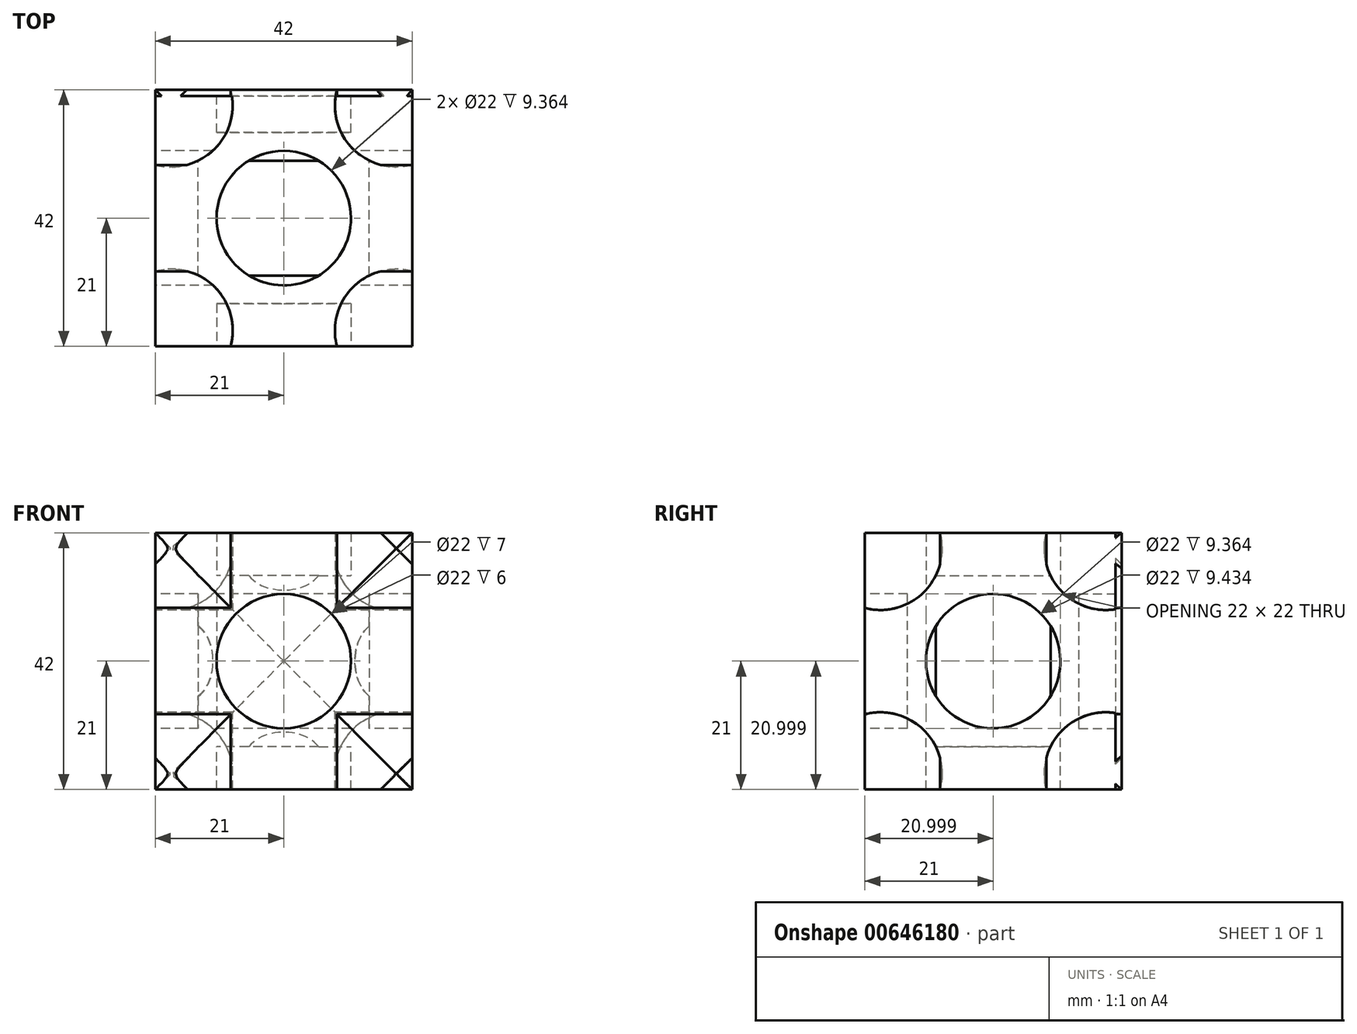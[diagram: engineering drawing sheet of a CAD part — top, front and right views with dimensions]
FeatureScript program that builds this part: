
annotation { "Feature Type Name" : "Feature", "Feature Type Description" : "" }
export const myFeature = defineFeature(function(context is Context, id is Id, definition is map)
    precondition{}
    {
        {
            var Q0;
            Q0=qCreatedBy(makeId("Top.planeOp"),FACE);
            var sketch = newSketch(context, id + "F0", { "sketchPlane" : qUnion([Q0])});
            skCircle(sketch, "E0", {"center": v(0, 0) * mm, "radius": 11 * mm});
            skPoint(sketch, "E1.0.midPoint", {"position": v(0, 21) * mm});
            skLineSegment(sketch, "E2", {"start": v(0, 21) * mm, "end": v(0, 11) * mm, "construction": true});
            skLineSegment(sketch, "E3", {"start": v(21, -0.1) * mm, "end": v(11, -0.1) * mm, "construction": true});
            skLineSegment(sketch, "E4", {"start": v(0, -11) * mm, "end": v(0, -21) * mm, "construction": true});
            skLineSegment(sketch, "E5", {"start": v(-21, -0.52) * mm, "end": v(-11, -0.27) * mm, "construction": true});
            skPoint(sketch, "E6.orphan", {"position": v(8.73, 20.99) * mm});
            skPoint(sketch, "E7.orphan", {"position": v(21.02, 8.65) * mm});
            skPoint(sketch, "E1.2.end.orphan", {"position": v(20.98, -8.85) * mm});
            skPoint(sketch, "E8.orphan", {"position": v(7.4, -20.44) * mm});
            skPoint(sketch, "E9.orphan", {"position": v(-7.4, -21.56) * mm});
            skPoint(sketch, "E10.orphan", {"position": v(-20.83, -9.53) * mm});
            skPoint(sketch, "E1.6.end.orphan", {"position": v(-21.15, 8.5) * mm});
            skPoint(sketch, "E1.0.start.orphan", {"position": v(-8.73, 21.01) * mm});
            skArc(sketch, "E11.cCircle", {"start": v(-19.25, 8.4) * mm, "mid": v(-21, 0) * mm, "end": v(-19.25, -8.39) * mm, "construction": true});
            skLineSegment(sketch, "E11.0", {"start": v(-8.7, 21) * mm, "end": v(8.7, 21) * mm});
            skLineSegment(sketch, "E11.2", {"start": v(21, 8.7) * mm, "end": v(21, -8.7) * mm});
            skLineSegment(sketch, "E11.4", {"start": v(8.7, -21) * mm, "end": v(-8.7, -21) * mm});
            skLineSegment(sketch, "E11.6", {"start": v(-21, -8.7) * mm, "end": v(-21, 8.7) * mm});
            skLineSegment(sketch, "E12", {"start": v(7.78, -7.78) * mm, "end": v(11.31, -11.31) * mm, "construction": true});
            skLineSegment(sketch, "E13", {"start": v(-7.4, -8.14) * mm, "end": v(-10.76, -11.84) * mm, "construction": true});
            skLineSegment(sketch, "E14", {"start": v(-7.83, 7.73) * mm, "end": v(-11.39, 11.24) * mm, "construction": true});
            skLineSegment(sketch, "E15", {"start": v(7.8, 7.76) * mm, "end": v(11.34, 11.3) * mm, "construction": true});
            skPoint(sketch, "E16.endSnap0", {"position": v(14.85, -14.85) * mm});
            skArc(sketch, "E17", {"start": v(-8.7, -21) * mm, "mid": v(-11.28, -11.28) * mm, "end": v(-21, -8.7) * mm});
            skArc(sketch, "E18", {"start": v(-21, 8.7) * mm, "mid": v(-11.31, 11.31) * mm, "end": v(-8.7, 21) * mm});
            skArc(sketch, "E19", {"start": v(21, -8.7) * mm, "mid": v(11.31, -11.31) * mm, "end": v(8.7, -21) * mm});
            skArc(sketch, "E20", {"start": v(8.7, 21) * mm, "mid": v(11.31, 11.31) * mm, "end": v(21, 8.7) * mm});
            skArc(sketch, "E21.trimOffspring", {"start": v(8.4, 19.25) * mm, "mid": v(0, 21) * mm, "end": v(-8.4, 19.25) * mm, "construction": true});
            skArc(sketch, "E22.trimOffspring", {"start": v(19.25, -8.4) * mm, "mid": v(21, 0) * mm, "end": v(19.25, 8.4) * mm, "construction": true});
            skArc(sketch, "E23.trimOffspring", {"start": v(-8.39, -19.25) * mm, "mid": v(0, -21) * mm, "end": v(8.4, -19.25) * mm, "construction": true});
            skSolve(sketch);
        }
        {
            var Q0;
            Q0=qCreatedBy(makeId("Right.planeOp"),FACE);
            var sketch = newSketch(context, id + "F1", { "sketchPlane" : qUnion([Q0])});
            skCircle(sketch, "E24", {"center": v(0, 0) * mm, "radius": 11 * mm});
            skCircle(sketch, "E25.cCircle", {"center": v(0, 0) * mm, "radius": 21 * mm, "construction": true});
            skLineSegment(sketch, "E25.0", {"start": v(-8.7, 21) * mm, "end": v(8.7, 21) * mm});
            skLineSegment(sketch, "E25.2", {"start": v(21, 8.7) * mm, "end": v(21, -8.7) * mm});
            skLineSegment(sketch, "E25.4", {"start": v(8.7, -21) * mm, "end": v(-8.7, -21) * mm});
            skLineSegment(sketch, "E25.6", {"start": v(-21, -8.7) * mm, "end": v(-21, 8.7) * mm});
            skPoint(sketch, "E25.0.midPoint", {"position": v(0, 21) * mm});
            skLineSegment(sketch, "E26", {"start": v(-14.85, 14.85) * mm, "end": v(-7.78, 7.78) * mm, "construction": true});
            skLineSegment(sketch, "E27", {"start": v(-14.85, -14.85) * mm, "end": v(-7.78, -7.78) * mm, "construction": true});
            skLineSegment(sketch, "E28", {"start": v(14.85, -14.85) * mm, "end": v(7.78, -7.78) * mm, "construction": true});
            skLineSegment(sketch, "E29", {"start": v(14.85, 14.85) * mm, "end": v(7.78, 7.78) * mm, "construction": true});
            skLineSegment(sketch, "E30", {"start": v(14.85, 14.85) * mm, "end": v(11.31, 11.31) * mm, "construction": true});
            skLineSegment(sketch, "E31", {"start": v(11.31, 11.31) * mm, "end": v(11.31, -11.31) * mm, "construction": true});
            skLineSegment(sketch, "E32", {"start": v(11.31, -11.31) * mm, "end": v(-11.31, -11.31) * mm, "construction": true});
            skLineSegment(sketch, "E33", {"start": v(-11.31, -11.31) * mm, "end": v(-11.31, 11.31) * mm, "construction": true});
            skLineSegment(sketch, "E34", {"start": v(-11.31, 11.31) * mm, "end": v(11.31, 11.31) * mm, "construction": true});
            skArc(sketch, "E35", {"start": v(21, -8.7) * mm, "mid": v(11.31, -11.31) * mm, "end": v(8.7, -21) * mm});
            skArc(sketch, "E36", {"start": v(8.7, 21) * mm, "mid": v(11.31, 11.31) * mm, "end": v(21, 8.7) * mm});
            skArc(sketch, "E37", {"start": v(-21, 8.7) * mm, "mid": v(-11.31, 11.31) * mm, "end": v(-8.7, 21) * mm});
            skArc(sketch, "E38", {"start": v(-8.7, -21) * mm, "mid": v(-11.31, -11.31) * mm, "end": v(-21, -8.7) * mm});
            skSolve(sketch);
        }
        {
            var Q0;
            Q0 = qSketchRegion(id + "F1", true);
            extrude(context, id + "F2", {"entities" : qUnion([Q0]), "depth" : 21 * mm, "offsetDistance" : 25 * mm});
        }
        {
            var Q0;
            Q0=makeQuery(id+"F2.opExtrude","CAP_FACE",FACE,{"disambiguationData":[OSD([sQuery(id+"F1.wireOp",EDGE,"E24"),sQuery(id+"F1.wireOp",EDGE,"E25.0"),sQuery(id+"F1.wireOp",EDGE,"E25.1"),sQuery(id+"F1.wireOp",EDGE,"E25.2"),sQuery(id+"F1.wireOp",EDGE,"E25.3"),sQuery(id+"F1.wireOp",EDGE,"E25.4"),sQuery(id+"F1.wireOp",EDGE,"E25.5"),sQuery(id+"F1.wireOp",EDGE,"E25.6"),sQuery(id+"F1.wireOp",EDGE,"E25.7")])],"isStart":true});
            extrude(context, id + "F3", {"entities" : qUnion([Q0]), "operationType" : NewBodyOperationType.ADD, "depth" : 21 * mm, "offsetDistance" : 25 * mm});
        }
        {
            var Q0;
            Q0 = qSketchRegion(id + "F0", true);
            extrude(context, id + "F4", {"entities" : qUnion([Q0]), "operationType" : NewBodyOperationType.ADD, "depth" : 21 * mm, "offsetDistance" : 25 * mm});
        }
        {
            var Q0;
            Q0 = qSketchRegion(id + "F0", true);
            extrude(context, id + "F5", {"entities" : qUnion([Q0]), "operationType" : NewBodyOperationType.ADD, "oppositeDirection" : true, "depth" : 21 * mm, "offsetDistance" : 25 * mm});
        }
        {
            var Q0;
            {var subQ0=sQuery(id+"F1.wireOp",EDGE,"E25.4");Q0=makeQuery(id+"F5.boolean.opBoolean","MERGE",FACE,{"derivedFrom":[makeQuery(id+"F3.boolean.opBoolean","MERGE",FACE,{"derivedFrom":[makeQuery(id+"F2.opExtrude","SWEPT_FACE",FACE,{"disambiguationData":[OSD([subQ0])]}),makeQuery(id+"F3.opExtrude","SWEPT_FACE",FACE,{"disambiguationData":[OSD([subQ0])]})]}),makeQuery(id+"F5.opExtrude","CAP_FACE",FACE,{"disambiguationData":[OSD([sQuery(id+"F0.wireOp",EDGE,"E0"),sQuery(id+"F0.wireOp",EDGE,"E11.0"),sQuery(id+"F0.wireOp",EDGE,"E11.1"),sQuery(id+"F0.wireOp",EDGE,"E11.2"),sQuery(id+"F0.wireOp",EDGE,"E11.3"),sQuery(id+"F0.wireOp",EDGE,"E11.4"),sQuery(id+"F0.wireOp",EDGE,"E11.5"),sQuery(id+"F0.wireOp",EDGE,"E11.6"),sQuery(id+"F0.wireOp",EDGE,"E11.7")])],"isStart":false})]});}
            var sketch = newSketch(context, id + "F6", { "sketchPlane" : qUnion([Q0])});
            skCircle(sketch, "E39", {"center": v(0, 0) * mm, "radius": 11 * mm});
            skSolve(sketch);
        }
        {
            var Q0;
            {var subQ1=sQuery(id+"F1.wireOp",EDGE,"E25.4");var subQ2=sQuery(id+"F1.wireOp",EDGE,"E25.3");var subQ3=makeQuery(id+"F3.boolean.opBoolean","MERGE",EDGE,{"derivedFrom":[makeQuery(id+"F2.opExtrude","SWEPT_EDGE",EDGE,{"disambiguationData":[OSD([subQ2,subQ1])]}),makeQuery(id+"F3.opExtrude","SWEPT_EDGE",EDGE,{"disambiguationData":[OSD([subQ2,subQ1])]})]});Q0=makeQuery(id+"F6.imprint","IMPRINT",FACE,{"disambiguationData":[TD([[makeQuery(id+"F6.imprint","IMPRINT",EDGE,{"derivedFrom":subQ3}),1.0]])]});}
            var Q1;
            {var subQ1=sQuery(id+"F1.wireOp",EDGE,"E25.5");var subQ2=sQuery(id+"F1.wireOp",EDGE,"E25.4");var subQ3=makeQuery(id+"F3.boolean.opBoolean","MERGE",EDGE,{"derivedFrom":[makeQuery(id+"F2.opExtrude","SWEPT_EDGE",EDGE,{"disambiguationData":[OSD([subQ2,subQ1])]}),makeQuery(id+"F3.opExtrude","SWEPT_EDGE",EDGE,{"disambiguationData":[OSD([subQ2,subQ1])]})]});Q1=makeQuery(id+"F6.imprint","IMPRINT",FACE,{"disambiguationData":[TD([[makeQuery(id+"F6.imprint","IMPRINT",EDGE,{"derivedFrom":subQ3}),-1.0]])]});}
            var Q2;
            {var subQ1=sQuery(id+"F1.wireOp",EDGE,"E25.4");var subQ2=sQuery(id+"F1.wireOp",EDGE,"E25.3");var subQ3=makeQuery(id+"F3.boolean.opBoolean","MERGE",EDGE,{"derivedFrom":[makeQuery(id+"F2.opExtrude","SWEPT_EDGE",EDGE,{"disambiguationData":[OSD([subQ2,subQ1])]}),makeQuery(id+"F3.opExtrude","SWEPT_EDGE",EDGE,{"disambiguationData":[OSD([subQ2,subQ1])]})]});Q2=makeQuery(id+"F6.imprint","IMPRINT",FACE,{"disambiguationData":[TD([[makeQuery(id+"F6.imprint","IMPRINT",EDGE,{"derivedFrom":subQ3}),-1.0]])]});}
            var Q3;
            Q3=sQuery(id+"F6.wireOp",EDGE,"E39");
            extrude(context, id + "F7", {"entities" : qUnion([Q0, Q1, Q2]), "operationType" : NewBodyOperationType.REMOVE, "surfaceEntities" : qUnion([Q3]), "oppositeDirection" : true, "depth" : 7 * mm, "offsetDistance" : 25 * mm});
        }
        {
            var Q0;
            {var subQ0=sQuery(id+"F0.wireOp",EDGE,"E11.4");var subQ1=sQuery(id+"F1.wireOp",EDGE,"E25.6");Q0=makeQuery(id+"F5.boolean.opBoolean","MERGE",FACE,{"derivedFrom":[makeQuery(id+"F4.boolean.opBoolean","MERGE",FACE,{"derivedFrom":[makeQuery(id+"F3.boolean.opBoolean","MERGE",FACE,{"derivedFrom":[makeQuery(id+"F2.opExtrude","SWEPT_FACE",FACE,{"disambiguationData":[OSD([subQ1])]}),makeQuery(id+"F3.opExtrude","SWEPT_FACE",FACE,{"disambiguationData":[OSD([subQ1])]})]}),makeQuery(id+"F4.opExtrude","SWEPT_FACE",FACE,{"disambiguationData":[OSD([subQ0])]})]}),makeQuery(id+"F5.opExtrude","SWEPT_FACE",FACE,{"disambiguationData":[OSD([subQ0])]})]});}
            var sketch = newSketch(context, id + "F8", { "sketchPlane" : qUnion([Q0])});
            skCircle(sketch, "E40", {"center": v(0, 0) * mm, "radius": 11 * mm});
            skSolve(sketch);
        }
        {
            var Q0;
            Q0 = qSketchRegion(id + "F8", true);
            extrude(context, id + "F9", {"entities" : qUnion([Q0]), "operationType" : NewBodyOperationType.REMOVE, "oppositeDirection" : true, "depth" : 7 * mm, "offsetDistance" : 25 * mm});
        }
        {
            var Q0;
            {var subQ0=sQuery(id+"F0.wireOp",EDGE,"E11.0");var subQ1=sQuery(id+"F1.wireOp",EDGE,"E25.2");Q0=makeQuery(id+"F5.boolean.opBoolean","MERGE",FACE,{"derivedFrom":[makeQuery(id+"F4.boolean.opBoolean","MERGE",FACE,{"derivedFrom":[makeQuery(id+"F3.boolean.opBoolean","MERGE",FACE,{"derivedFrom":[makeQuery(id+"F2.opExtrude","SWEPT_FACE",FACE,{"disambiguationData":[OSD([subQ1])]}),makeQuery(id+"F3.opExtrude","SWEPT_FACE",FACE,{"disambiguationData":[OSD([subQ1])]})]}),makeQuery(id+"F4.opExtrude","SWEPT_FACE",FACE,{"disambiguationData":[OSD([subQ0])]})]}),makeQuery(id+"F5.opExtrude","SWEPT_FACE",FACE,{"disambiguationData":[OSD([subQ0])]})]});}
            var sketch = newSketch(context, id + "F10", { "sketchPlane" : qUnion([Q0])});
            skCircle(sketch, "E41", {"center": v(0, 0) * mm, "radius": 11 * mm});
            skSolve(sketch);
        }
        {
            var Q0;
            {var subQ0=sQuery(id+"F0.wireOp",EDGE,"E11.2");Q0=makeQuery(id+"F5.boolean.opBoolean","MERGE",FACE,{"derivedFrom":[makeQuery(id+"F4.boolean.opBoolean","MERGE",FACE,{"derivedFrom":[makeQuery(id+"F2.opExtrude","CAP_FACE",FACE,{"disambiguationData":[OSD([sQuery(id+"F1.wireOp",EDGE,"E24"),sQuery(id+"F1.wireOp",EDGE,"E25.0"),sQuery(id+"F1.wireOp",EDGE,"E25.1"),sQuery(id+"F1.wireOp",EDGE,"E25.2"),sQuery(id+"F1.wireOp",EDGE,"E25.3"),sQuery(id+"F1.wireOp",EDGE,"E25.4"),sQuery(id+"F1.wireOp",EDGE,"E25.5"),sQuery(id+"F1.wireOp",EDGE,"E25.6"),sQuery(id+"F1.wireOp",EDGE,"E25.7")])],"isStart":false}),makeQuery(id+"F4.opExtrude","SWEPT_FACE",FACE,{"disambiguationData":[OSD([subQ0])]})]}),makeQuery(id+"F5.opExtrude","SWEPT_FACE",FACE,{"disambiguationData":[OSD([subQ0])]})]});}
            var sketch = newSketch(context, id + "F11", { "sketchPlane" : qUnion([Q0])});
            skCircle(sketch, "E42", {"center": v(0, 0) * mm, "radius": 11 * mm});
            skSolve(sketch);
        }
        {
            var Q0;
            {var subQ0=sQuery(id+"F1.wireOp",EDGE,"E25.0");Q0=makeQuery(id+"F4.boolean.opBoolean","MERGE",FACE,{"derivedFrom":[makeQuery(id+"F3.boolean.opBoolean","MERGE",FACE,{"derivedFrom":[makeQuery(id+"F2.opExtrude","SWEPT_FACE",FACE,{"disambiguationData":[OSD([subQ0])]}),makeQuery(id+"F3.opExtrude","SWEPT_FACE",FACE,{"disambiguationData":[OSD([subQ0])]})]}),makeQuery(id+"F4.opExtrude","CAP_FACE",FACE,{"disambiguationData":[OSD([sQuery(id+"F0.wireOp",EDGE,"E0"),sQuery(id+"F0.wireOp",EDGE,"E11.0"),sQuery(id+"F0.wireOp",EDGE,"E11.1"),sQuery(id+"F0.wireOp",EDGE,"E11.2"),sQuery(id+"F0.wireOp",EDGE,"E11.3"),sQuery(id+"F0.wireOp",EDGE,"E11.4"),sQuery(id+"F0.wireOp",EDGE,"E11.5"),sQuery(id+"F0.wireOp",EDGE,"E11.6"),sQuery(id+"F0.wireOp",EDGE,"E11.7")])],"isStart":false})]});}
            var sketch = newSketch(context, id + "F12", { "sketchPlane" : qUnion([Q0])});
            skCircle(sketch, "E43", {"center": v(0, 0) * mm, "radius": 11 * mm});
            skSolve(sketch);
        }
        {
            var Q0;
            {var subQ0=sQuery(id+"F0.wireOp",EDGE,"E11.6");Q0=makeQuery(id+"F5.boolean.opBoolean","MERGE",FACE,{"derivedFrom":[makeQuery(id+"F4.boolean.opBoolean","MERGE",FACE,{"derivedFrom":[makeQuery(id+"F3.opExtrude","CAP_FACE",FACE,{"disambiguationData":[OSD([sQuery(id+"F1.wireOp",EDGE,"E24"),sQuery(id+"F1.wireOp",EDGE,"E25.0"),sQuery(id+"F1.wireOp",EDGE,"E25.1"),sQuery(id+"F1.wireOp",EDGE,"E25.2"),sQuery(id+"F1.wireOp",EDGE,"E25.3"),sQuery(id+"F1.wireOp",EDGE,"E25.4"),sQuery(id+"F1.wireOp",EDGE,"E25.5"),sQuery(id+"F1.wireOp",EDGE,"E25.6"),sQuery(id+"F1.wireOp",EDGE,"E25.7")])],"isStart":false}),makeQuery(id+"F4.opExtrude","SWEPT_FACE",FACE,{"disambiguationData":[OSD([subQ0])]})]}),makeQuery(id+"F5.opExtrude","SWEPT_FACE",FACE,{"disambiguationData":[OSD([subQ0])]})]});}
            var sketch = newSketch(context, id + "F13", { "sketchPlane" : qUnion([Q0])});
            skCircle(sketch, "E44", {"center": v(0, 0) * mm, "radius": 11 * mm});
            skSolve(sketch);
        }
        {
            var Q0;
            Q0 = qSketchRegion(id + "F13", true);
            extrude(context, id + "F14", {"entities" : qUnion([Q0]), "operationType" : NewBodyOperationType.REMOVE, "oppositeDirection" : true, "depth" : 7 * mm, "offsetDistance" : 25 * mm});
        }
        {
            var Q0;
            Q0 = qSketchRegion(id + "F10", true);
            extrude(context, id + "F15", {"entities" : qUnion([Q0]), "operationType" : NewBodyOperationType.REMOVE, "oppositeDirection" : true, "depth" : 7 * mm, "offsetDistance" : 25 * mm});
        }
        {
            var Q0;
            Q0 = qSketchRegion(id + "F11", true);
            extrude(context, id + "F16", {"entities" : qUnion([Q0]), "operationType" : NewBodyOperationType.REMOVE, "oppositeDirection" : true, "depth" : 7 * mm, "offsetDistance" : 25 * mm});
        }
        {
            var Q0;
            Q0 = qSketchRegion(id + "F12", true);
            extrude(context, id + "F17", {"entities" : qUnion([Q0]), "operationType" : NewBodyOperationType.REMOVE, "oppositeDirection" : true, "depth" : 7 * mm, "offsetDistance" : 25 * mm});
        }
        {
            var Q0;
            {var subQ0=sQuery(id+"F1.wireOp",EDGE,"E25.4");Q0=makeQuery(id+"F5.boolean.opBoolean","MERGE",FACE,{"derivedFrom":[makeQuery(id+"F3.boolean.opBoolean","MERGE",FACE,{"derivedFrom":[makeQuery(id+"F2.opExtrude","SWEPT_FACE",FACE,{"disambiguationData":[OSD([subQ0])]}),makeQuery(id+"F3.opExtrude","SWEPT_FACE",FACE,{"disambiguationData":[OSD([subQ0])]})]}),makeQuery(id+"F5.opExtrude","CAP_FACE",FACE,{"disambiguationData":[OSD([sQuery(id+"F0.wireOp",EDGE,"E0"),sQuery(id+"F0.wireOp",EDGE,"E11.0"),sQuery(id+"F0.wireOp",EDGE,"E11.2"),sQuery(id+"F0.wireOp",EDGE,"E11.4"),sQuery(id+"F0.wireOp",EDGE,"E11.6"),sQuery(id+"F0.wireOp",EDGE,"E17"),sQuery(id+"F0.wireOp",EDGE,"E18"),sQuery(id+"F0.wireOp",EDGE,"E19"),sQuery(id+"F0.wireOp",EDGE,"E20")])],"isStart":false})]});}
            var sketch = newSketch(context, id + "F18", { "sketchPlane" : qUnion([Q0])});
            skCircle(sketch, "E45", {"center": v(0, 0) * mm, "radius": 11 * mm});
            skSolve(sketch);
        }
        {
            var Q0;
            Q0 = qSketchRegion(id + "F18", true);
            extrude(context, id + "F19", {"entities" : qUnion([Q0]), "operationType" : NewBodyOperationType.REMOVE, "oppositeDirection" : true, "depth" : 7 * mm, "offsetDistance" : 25 * mm});
        }
        {
            var Q0;
            Q0=makeQuery(id+"F10.imprint","IMPRINT",FACE,{"disambiguationData":[TD([[makeQuery(id+"F10.imprint","IMPRINT",EDGE,{"derivedFrom":sQuery(id+"F10.wireOp",EDGE,"E41")}),-1.0]])]});
            var sketch = newSketch(context, id + "F20", { "sketchPlane" : qUnion([Q0])});
            skLineSegment(sketch, "E46.0", {"start": v(-8.7, 21) * mm, "end": v(8.7, 21) * mm, "construction": true});
            skLineSegment(sketch, "E46.1", {"start": v(8.7, 21) * mm, "end": v(21, 8.7) * mm, "construction": true});
            skLineSegment(sketch, "E46.2", {"start": v(21, 8.7) * mm, "end": v(21, -8.7) * mm, "construction": true});
            skLineSegment(sketch, "E46.3", {"start": v(21, -8.7) * mm, "end": v(8.7, -21) * mm, "construction": true});
            skLineSegment(sketch, "E46.4", {"start": v(8.7, -21) * mm, "end": v(-8.7, -21) * mm, "construction": true});
            skLineSegment(sketch, "E46.5", {"start": v(-8.7, -21) * mm, "end": v(-21, -8.7) * mm, "construction": true});
            skLineSegment(sketch, "E46.6", {"start": v(-21, -8.7) * mm, "end": v(-21, 8.7) * mm, "construction": true});
            skLineSegment(sketch, "E46.7", {"start": v(-14.85, 14.85) * mm, "end": v(-8.7, 21) * mm, "construction": true});
            skPoint(sketch, "E46.0.midPoint", {"position": v(0, 21) * mm});
            skLineSegment(sketch, "E47", {"start": v(-7.42, 7.42) * mm, "end": v(-11.14, 11.14) * mm, "construction": true});
            skArc(sketch, "E48", {"start": v(-21, 8.7) * mm, "mid": v(-11.14, 11.14) * mm, "end": v(-8.7, 21) * mm});
            skPoint(sketch, "E49.end.orphan", {"position": v(14.85, 14.85) * mm});
            skPoint(sketch, "E50.start.orphan", {"position": v(14.85, -14.85) * mm});
            skPoint(sketch, "E51.end.orphan", {"position": v(-14.85, -14.85) * mm});
            skLineSegment(sketch, "E52", {"start": v(11.14, 11.14) * mm, "end": v(11.31, 11.31) * mm, "construction": true});
            skLineSegment(sketch, "E53", {"start": v(11.14, 11.14) * mm, "end": v(11.31, 11.14) * mm, "construction": true});
            skPoint(sketch, "E54.orphan", {"position": v(11.31, 11.31) * mm});
            skPoint(sketch, "E55.orphan", {"position": v(7.78, 7.78) * mm});
            skLineSegment(sketch, "E56", {"start": v(-11.14, 11.14) * mm, "end": v(11.31, 11.14) * mm, "construction": true});
            skLineSegment(sketch, "E57", {"start": v(-11.14, 11.14) * mm, "end": v(-11.14, -11.31) * mm, "construction": true});
            skLineSegment(sketch, "E58", {"start": v(-11.14, 11.14) * mm, "end": v(11.31, -11.31) * mm, "construction": true});
            skLineSegment(sketch, "E59", {"start": v(11.31, 11.14) * mm, "end": v(11.31, -11.31) * mm, "construction": true});
            skLineSegment(sketch, "E60", {"start": v(11.31, -11.31) * mm, "end": v(-11.14, -11.31) * mm, "construction": true});
            skArc(sketch, "E61", {"start": v(8.7, 21) * mm, "mid": v(11.31, 11.31) * mm, "end": v(21, 8.7) * mm});
            skArc(sketch, "E62", {"start": v(21, -8.7) * mm, "mid": v(11.31, -11.31) * mm, "end": v(8.7, -21) * mm});
            skArc(sketch, "E63", {"start": v(-8.7, -21) * mm, "mid": v(-11.22, -11.22) * mm, "end": v(-21, -8.7) * mm});
            skArc(sketch, "E64.trimOffspring", {"start": v(19.25, -8.4) * mm, "mid": v(11.83, 17.35) * mm, "end": v(-14.85, 14.85) * mm, "construction": true});
            skLineSegment(sketch, "E65", {"start": v(-21, 8.7) * mm, "end": v(-21, -8.7) * mm});
            skLineSegment(sketch, "E66", {"start": v(-8.7, 21) * mm, "end": v(8.7, 21) * mm});
            skLineSegment(sketch, "E67", {"start": v(8.7, -21) * mm, "end": v(-8.7, -21) * mm});
            skLineSegment(sketch, "E68", {"start": v(21, 8.7) * mm, "end": v(21, -8.7) * mm});
            skSolve(sketch);
        }
        {
            var Q0;
            Q0 = qSketchRegion(id + "F20", true);
            extrude(context, id + "F21", {"entities" : qUnion([Q0]), "operationType" : NewBodyOperationType.ADD, "oppositeDirection" : true, "depth" : 1 * mm, "offsetDistance" : 25 * mm});
        }
    });
